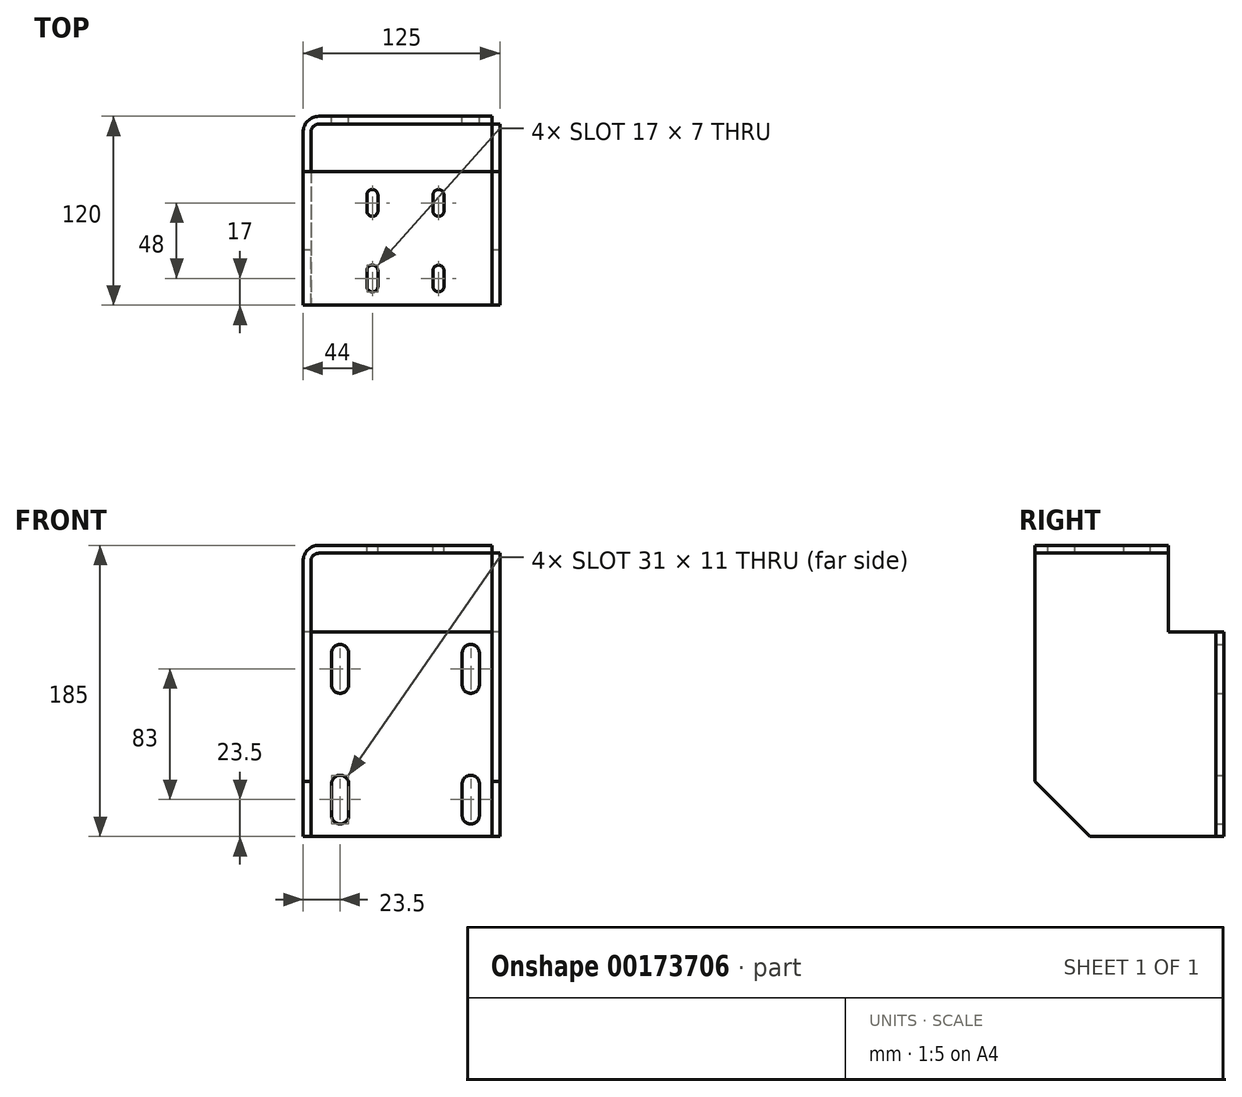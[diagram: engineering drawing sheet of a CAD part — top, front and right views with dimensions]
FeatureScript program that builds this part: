
annotation { "Feature Type Name" : "Feature", "Feature Type Description" : "" }
export const myFeature = defineFeature(function(context is Context, id is Id, definition is map)
    precondition{}
    {
        {
            var Q0;
            Q0=qCreatedBy(makeId("Front.planeOp"),FACE);
            var sketch = newSketch(context, id + "F0", { "sketchPlane" : qUnion([Q0])});
            skLineSegment(sketch, "E0.bottom", {"start": v(55, 65) * mm, "end": v(-55, 65) * mm});
            skLineSegment(sketch, "E0.top", {"start": v(55, -65) * mm, "end": v(-55, -65) * mm});
            skLineSegment(sketch, "E0.left", {"start": v(55, 65) * mm, "end": v(55, -65) * mm});
            skLineSegment(sketch, "E0.right", {"start": v(-55, 65) * mm, "end": v(-55, -65) * mm});
            skPoint(sketch, "E0.middle", {"position": v(0, 0) * mm});
            skLineSegment(sketch, "E1.bottom", {"start": v(-36, 31.5) * mm, "end": v(-47, 31.5) * mm, "construction": true});
            skLineSegment(sketch, "E1.top", {"start": v(-36, 51.5) * mm, "end": v(-47, 51.5) * mm, "construction": true});
            skLineSegment(sketch, "E1.left", {"start": v(-36, 31.5) * mm, "end": v(-36, 51.5) * mm});
            skLineSegment(sketch, "E1.right", {"start": v(-47, 31.5) * mm, "end": v(-47, 51.5) * mm});
            skPoint(sketch, "E1.middle", {"position": v(-41.5, 41.5) * mm});
            skLineSegment(sketch, "E2", {"start": v(0, 0) * mm, "end": v(0, 47.19) * mm, "construction": true});
            skLineSegment(sketch, "E3", {"start": v(0, 0) * mm, "end": v(29.14, 0) * mm, "construction": true});
            skArc(sketch, "E4", {"start": v(-47, 51.5) * mm, "mid": v(-41.5, 57) * mm, "end": v(-36, 51.5) * mm});
            skArc(sketch, "E5", {"start": v(-47, 31.5) * mm, "mid": v(-41.5, 26) * mm, "end": v(-36, 31.5) * mm});
            skLineSegment(sketch, "E6.MirrorCS", {"start": v(36, 31.5) * mm, "end": v(36, 51.5) * mm});
            skArc(sketch, "E7.MirrorCS", {"start": v(47, 31.5) * mm, "mid": v(41.5, 26) * mm, "end": v(36, 31.5) * mm});
            skLineSegment(sketch, "E8.MirrorCS", {"start": v(47, 31.5) * mm, "end": v(47, 51.5) * mm});
            skArc(sketch, "E9.MirrorCS", {"start": v(47, 51.5) * mm, "mid": v(41.5, 57) * mm, "end": v(36, 51.5) * mm});
            skArc(sketch, "E10.MirrorCS", {"start": v(47, -31.5) * mm, "mid": v(41.5, -26) * mm, "end": v(36, -31.5) * mm});
            skLineSegment(sketch, "E11.MirrorCS", {"start": v(47, -31.5) * mm, "end": v(47, -51.5) * mm});
            skLineSegment(sketch, "E12.MirrorCS", {"start": v(36, -31.5) * mm, "end": v(36, -51.5) * mm});
            skArc(sketch, "E13.MirrorCS", {"start": v(47, -51.5) * mm, "mid": v(41.5, -57) * mm, "end": v(36, -51.5) * mm});
            skArc(sketch, "E14.MirrorCS", {"start": v(-47, -51.5) * mm, "mid": v(-41.5, -57) * mm, "end": v(-36, -51.5) * mm});
            skLineSegment(sketch, "E15.MirrorCS", {"start": v(-47, -31.5) * mm, "end": v(-47, -51.5) * mm});
            skLineSegment(sketch, "E16.MirrorCS", {"start": v(-36, -31.5) * mm, "end": v(-36, -51.5) * mm});
            skArc(sketch, "E17.MirrorCS", {"start": v(-47, -31.5) * mm, "mid": v(-41.5, -26) * mm, "end": v(-36, -31.5) * mm});
            skSolve(sketch);
        }
        {
            var Q0;
            Q0=qSketchRegion(id+"F0",true);
            extrude(context, id + "F1", {"entities" : qUnion([Q0]), "depth" : 5 * mm});
        }
        {
            var Q0;
            Q0=makeQuery(id+"F1.opExtrude","SWEPT_FACE",FACE,{"disambiguationData":[OSD([sQuery(id+"F0.wireOp",EDGE,"E0.bottom")])]});
            var sketch = newSketch(context, id + "F2", { "sketchPlane" : qUnion([Q0])});
            skLineSegment(sketch, "E18.0", {"start": v(-55, -5) * mm, "end": v(-55, 0) * mm});
            skArc(sketch, "E19", {"start": v(-55, 0) * mm, "mid": v(-62.07, -2.93) * mm, "end": v(-65, -10) * mm});
            skArc(sketch, "E20", {"start": v(-55, -5) * mm, "mid": v(-58.54, -6.46) * mm, "end": v(-60, -10) * mm});
            skLineSegment(sketch, "E21", {"start": v(-60, -10) * mm, "end": v(-60, -120) * mm});
            skLineSegment(sketch, "E22", {"start": v(-60, -120) * mm, "end": v(-65, -120) * mm});
            skLineSegment(sketch, "E23", {"start": v(-65, -120) * mm, "end": v(-65, -10) * mm});
            skSolve(sketch);
        }
        {
            var Q0;
            Q0=qSketchRegion(id+"F2",true);
            var Q1;
            Q1=makeQuery(id+"F1.opExtrude","SWEPT_FACE",FACE,{"disambiguationData":[OSD([sQuery(id+"F0.wireOp",EDGE,"E0.top")])]});
            extrude(context, id + "F3", {"entities" : qUnion([Q0]), "operationType" : NewBodyOperationType.ADD, "endBound" : BoundingType.UP_TO_SURFACE, "oppositeDirection" : true, "endBoundEntityFace" : qUnion([Q1]), "depth" : 25 * mm});
        }
        {
            var Q0;
            Q0=makeQuery(id+"F3.opExtrude","SWEPT_FACE",FACE,{"disambiguationData":[OSD([sQuery(id+"F2.wireOp",EDGE,"E22")])]});
            var sketch = newSketch(context, id + "F4", { "sketchPlane" : qUnion([Q0])});
            skLineSegment(sketch, "E24.0", {"start": v(-60, 65) * mm, "end": v(-65, 65) * mm});
            skLineSegment(sketch, "E25", {"start": v(-65, 65) * mm, "end": v(-65, 110) * mm});
            skLineSegment(sketch, "E26", {"start": v(-60, 65) * mm, "end": v(-60, 110) * mm});
            skArc(sketch, "E27", {"start": v(-55, 120) * mm, "mid": v(-62.07, 117.07) * mm, "end": v(-65, 110) * mm});
            skArc(sketch, "E28", {"start": v(-55, 115) * mm, "mid": v(-58.54, 113.54) * mm, "end": v(-60, 110) * mm});
            skLineSegment(sketch, "E29", {"start": v(-55, 120) * mm, "end": v(55, 120) * mm});
            skLineSegment(sketch, "E30", {"start": v(55, 120) * mm, "end": v(55, 115) * mm});
            skLineSegment(sketch, "E31", {"start": v(55, 115) * mm, "end": v(-55, 115) * mm});
            skSolve(sketch);
        }
        {
            var Q0;
            Q0=qSketchRegion(id+"F4",true);
            extrude(context, id + "F5", {"entities" : qUnion([Q0]), "operationType" : NewBodyOperationType.ADD, "oppositeDirection" : true, "depth" : 85 * mm});
        }
        {
            var Q0;
            Q0=makeQuery(id+"F5.opExtrude","SWEPT_FACE",FACE,{"disambiguationData":[OSD([sQuery(id+"F4.wireOp",EDGE,"E29")])]});
            var sketch = newSketch(context, id + "F6", { "sketchPlane" : qUnion([Q0])});
            skLineSegment(sketch, "E32.bottom", {"start": v(17.5, -60) * mm, "end": v(24.5, -60) * mm, "construction": true});
            skLineSegment(sketch, "E32.top", {"start": v(17.5, -50) * mm, "end": v(24.5, -50) * mm, "construction": true});
            skLineSegment(sketch, "E32.left", {"start": v(17.5, -60) * mm, "end": v(17.5, -50) * mm});
            skLineSegment(sketch, "E32.right", {"start": v(24.5, -60) * mm, "end": v(24.5, -50) * mm});
            skPoint(sketch, "E32.middle", {"position": v(21, -55) * mm});
            skArc(sketch, "E33", {"start": v(17.5, -60) * mm, "mid": v(21, -63.5) * mm, "end": v(24.5, -60) * mm});
            skArc(sketch, "E34", {"start": v(24.5, -50) * mm, "mid": v(21, -46.5) * mm, "end": v(17.5, -50) * mm});
            skArc(sketch, "E35.0.1.0", {"start": v(17.5, -108) * mm, "mid": v(21, -111.5) * mm, "end": v(24.5, -108) * mm});
            skLineSegment(sketch, "E35.0.1.1", {"start": v(24.5, -108) * mm, "end": v(24.5, -98) * mm});
            skLineSegment(sketch, "E35.0.1.2", {"start": v(17.5, -108) * mm, "end": v(17.5, -98) * mm});
            skArc(sketch, "E35.0.1.3", {"start": v(24.5, -98) * mm, "mid": v(21, -94.5) * mm, "end": v(17.5, -98) * mm});
            skArc(sketch, "E35.1.0.0", {"start": v(-24.5, -60) * mm, "mid": v(-21, -63.5) * mm, "end": v(-17.5, -60) * mm});
            skLineSegment(sketch, "E35.1.0.1", {"start": v(-17.5, -60) * mm, "end": v(-17.5, -50) * mm});
            skLineSegment(sketch, "E35.1.0.2", {"start": v(-24.5, -60) * mm, "end": v(-24.5, -50) * mm});
            skArc(sketch, "E35.1.0.3", {"start": v(-17.5, -50) * mm, "mid": v(-21, -46.5) * mm, "end": v(-24.5, -50) * mm});
            skArc(sketch, "E35.1.1.0", {"start": v(-24.5, -108) * mm, "mid": v(-21, -111.5) * mm, "end": v(-17.5, -108) * mm});
            skLineSegment(sketch, "E35.1.1.1", {"start": v(-17.5, -108) * mm, "end": v(-17.5, -98) * mm});
            skLineSegment(sketch, "E35.1.1.2", {"start": v(-24.5, -108) * mm, "end": v(-24.5, -98) * mm});
            skArc(sketch, "E35.1.1.3", {"start": v(-17.5, -98) * mm, "mid": v(-21, -94.5) * mm, "end": v(-24.5, -98) * mm});
            skLineSegment(sketch, "E35.direction1", {"start": v(17.5, -60) * mm, "end": v(-24.5, -60) * mm, "construction": true});
            skLineSegment(sketch, "E35.direction2", {"start": v(17.5, -60) * mm, "end": v(17.5, -108) * mm, "construction": true});
            skSolve(sketch);
        }
        {
            var Q0;
            Q0=qSketchRegion(id+"F6",true);
            extrude(context, id + "F7", {"entities" : qUnion([Q0]), "operationType" : NewBodyOperationType.REMOVE, "endBound" : BoundingType.THROUGH_ALL, "oppositeDirection" : true, "depth" : 25 * mm});
        }
        {
            var Q0;
            Q0=makeQuery(id+"F1.opExtrude","SWEPT_FACE",FACE,{"disambiguationData":[OSD([sQuery(id+"F0.wireOp",EDGE,"E0.left")])]});
            var sketch = newSketch(context, id + "F8", { "sketchPlane" : qUnion([Q0])});
            skLineSegment(sketch, "E36", {"start": v(-5, -65) * mm, "end": v(-5, 65) * mm});
            skLineSegment(sketch, "E37", {"start": v(-5, 65) * mm, "end": v(-35, 65) * mm});
            skLineSegment(sketch, "E38", {"start": v(-35, 65) * mm, "end": v(-35, 115) * mm});
            skLineSegment(sketch, "E39", {"start": v(-35, 115) * mm, "end": v(-120, 115) * mm});
            skLineSegment(sketch, "E40", {"start": v(-120, 115) * mm, "end": v(-120, -65) * mm});
            skLineSegment(sketch, "E41", {"start": v(-120, -65) * mm, "end": v(-5, -65) * mm});
            skSolve(sketch);
        }
        {
            var Q0;
            Q0=qSketchRegion(id+"F8",true);
            extrude(context, id + "F9", {"entities" : qUnion([Q0]), "depth" : 5 * mm});
        }
        {
            var Q0;
            Q0=makeQuery(id+"F3.opExtrude","CAP_EDGE",EDGE,{"disambiguationData":[OSD([sQuery(id+"F2.wireOp",EDGE,"E22")])],"isStart":false});
            var Q1;
            Q1=makeQuery(id+"F9.opExtrude","SWEPT_EDGE",EDGE,{"disambiguationData":[OSD([sQuery(id+"F8.wireOp",EDGE,"E40"),sQuery(id+"F8.wireOp",EDGE,"E41")])]});
            chamfer(context, id + "F10", {"entities" : qUnion([Q0, Q1]), "width" : 35 * mm, "tangentPropagation" : true});
        }
    });
